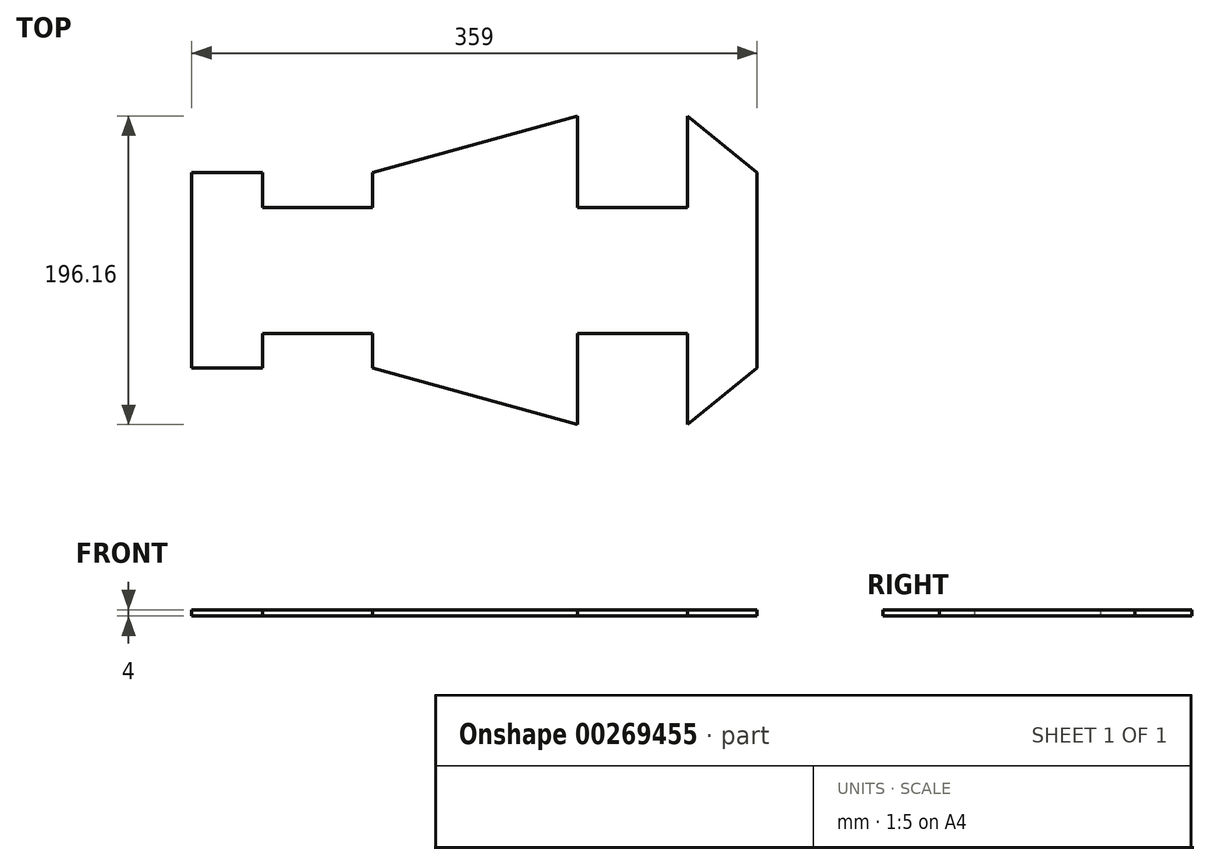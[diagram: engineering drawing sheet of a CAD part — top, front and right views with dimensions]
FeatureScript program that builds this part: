
annotation { "Feature Type Name" : "Feature", "Feature Type Description" : "" }
export const myFeature = defineFeature(function(context is Context, id is Id, definition is map)
    precondition{}
    {
        {
            var Q0;
            Q0=qCreatedBy(makeId("Top.planeOp"),FACE);
            var sketch = newSketch(context, id + "F0", { "sketchPlane" : qUnion([Q0])});
            skLineSegment(sketch, "E0", {"start": v(0, 0) * mm, "end": v(0, 62) * mm});
            skLineSegment(sketch, "E1", {"start": v(45, 62) * mm, "end": v(0, 62) * mm});
            skLineSegment(sketch, "E2", {"start": v(45, 62) * mm, "end": v(45, 40) * mm});
            skLineSegment(sketch, "E3", {"start": v(45, 40) * mm, "end": v(115, 40) * mm});
            skLineSegment(sketch, "E4", {"start": v(115, 40) * mm, "end": v(115, 62) * mm});
            skLineSegment(sketch, "E5", {"start": v(115, 62) * mm, "end": v(245, 98.08) * mm});
            skLineSegment(sketch, "E6", {"start": v(245, 98.08) * mm, "end": v(245, 40) * mm});
            skLineSegment(sketch, "E7", {"start": v(245, 40) * mm, "end": v(315, 40) * mm});
            skLineSegment(sketch, "E8", {"start": v(315, 40) * mm, "end": v(315, 98.08) * mm});
            skLineSegment(sketch, "E9", {"start": v(315, 98.08) * mm, "end": v(359, 62) * mm});
            skLineSegment(sketch, "E10", {"start": v(359, 62) * mm, "end": v(359, 0) * mm});
            skLineSegment(sketch, "E11.MirrorCS", {"start": v(45, -62) * mm, "end": v(45, -40) * mm});
            skLineSegment(sketch, "E12.MirrorCS", {"start": v(0, 0) * mm, "end": v(0, -62) * mm});
            skLineSegment(sketch, "E13.MirrorCS", {"start": v(115, -62) * mm, "end": v(245, -98.08) * mm});
            skLineSegment(sketch, "E14.MirrorCS", {"start": v(245, -98.08) * mm, "end": v(245, -40) * mm});
            skLineSegment(sketch, "E15.MirrorCS", {"start": v(45, -40) * mm, "end": v(115, -40) * mm});
            skLineSegment(sketch, "E16.MirrorCS", {"start": v(245, -40) * mm, "end": v(315, -40) * mm});
            skLineSegment(sketch, "E17.MirrorCS", {"start": v(315, -40) * mm, "end": v(315, -98.08) * mm});
            skLineSegment(sketch, "E18.MirrorCS", {"start": v(115, -40) * mm, "end": v(115, -62) * mm});
            skLineSegment(sketch, "E19.MirrorCS", {"start": v(315, -98.08) * mm, "end": v(359, -62) * mm});
            skLineSegment(sketch, "E20.MirrorCS", {"start": v(359, -62) * mm, "end": v(359, 0) * mm});
            skLineSegment(sketch, "E21.MirrorCS", {"start": v(45, -62) * mm, "end": v(0, -62) * mm});
            skSolve(sketch);
        }
        {
            var Q0;
            Q0=makeQuery(id+"F0.imprint","IMPRINT",FACE,{"disambiguationData":[TD([[makeQuery(id+"F0.imprint","IMPRINT",EDGE,{"derivedFrom":sQuery(id+"F0.wireOp",EDGE,"E0")}),-1.0]])]});
            extrude(context, id + "F1", {"entities" : qUnion([Q0]), "endBound" : BoundingType.SYMMETRIC, "depth" : 4 * mm});
        }
    });
